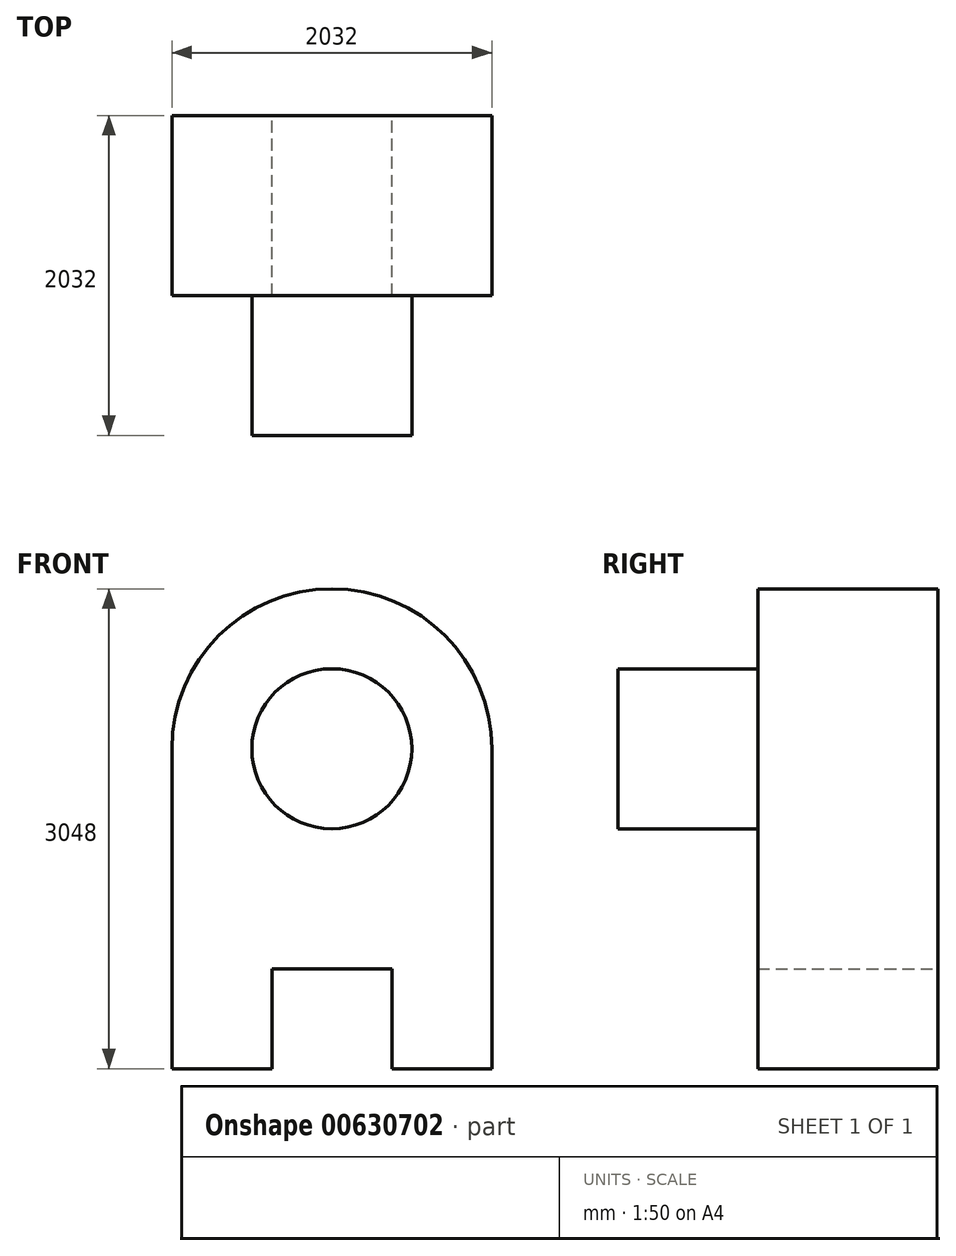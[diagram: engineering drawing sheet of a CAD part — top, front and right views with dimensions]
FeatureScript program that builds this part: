
annotation { "Feature Type Name" : "Feature", "Feature Type Description" : "" }
export const myFeature = defineFeature(function(context is Context, id is Id, definition is map)
    precondition{}
    {
        {
            var Q0;
            Q0=qCreatedBy(makeId("Front.planeOp"),FACE);
            var sketch = newSketch(context, id + "F0", { "sketchPlane" : qUnion([Q0])});
            skLineSegment(sketch, "E0.bottom", {"start": v(-1016, -1016) * mm, "end": v(-381, -1016) * mm});
            skLineSegment(sketch, "E0.left", {"start": v(-1016, -1016) * mm, "end": v(-1016, 1016) * mm});
            skLineSegment(sketch, "E0.right", {"start": v(1016, -1016) * mm, "end": v(1016, 1016) * mm});
            skPoint(sketch, "E0.middle", {"position": v(0, 0) * mm});
            skArc(sketch, "E1", {"start": v(1016, 1016) * mm, "mid": v(0, 2032) * mm, "end": v(-1016, 1016) * mm});
            skLineSegment(sketch, "E2.top", {"start": v(-381, -381) * mm, "end": v(381, -381) * mm});
            skLineSegment(sketch, "E2.left", {"start": v(-381, -1016) * mm, "end": v(-381, -381) * mm});
            skLineSegment(sketch, "E2.right", {"start": v(381, -1016) * mm, "end": v(381, -381) * mm});
            skPoint(sketch, "E2.middle", {"position": v(0, -1016) * mm});
            skPoint(sketch, "E2.bottom.end.orphan", {"position": v(381, -1651) * mm});
            skLineSegment(sketch, "E3.trimOffspring", {"start": v(381, -1016) * mm, "end": v(1016, -1016) * mm});
            skPoint(sketch, "E4.orphan", {"position": v(-381, -1651) * mm});
            skSolve(sketch);
        }
        {
            var Q0;
            Q0 = qSketchRegion(id + "F0", true);
            extrude(context, id + "F1", {"entities" : qUnion([Q0]), "depth" : 1143 * mm, "offsetDistance" : 25.4 * mm});
        }
        {
            var Q0;
            Q0=makeQuery(id+"F1.opExtrude","CAP_FACE",FACE,{"disambiguationData":[OSD([sQuery(id+"F0.wireOp",EDGE,"E0.bottom"),sQuery(id+"F0.wireOp",EDGE,"E0.left"),sQuery(id+"F0.wireOp",EDGE,"E0.right"),sQuery(id+"F0.wireOp",EDGE,"E1"),sQuery(id+"F0.wireOp",EDGE,"E2.top"),sQuery(id+"F0.wireOp",EDGE,"E2.left"),sQuery(id+"F0.wireOp",EDGE,"E2.right"),sQuery(id+"F0.wireOp",EDGE,"E3.trimOffspring")])],"isStart":false});
            var sketch = newSketch(context, id + "F2", { "sketchPlane" : qUnion([Q0])});
            skCircle(sketch, "E5", {"center": v(0, 1016) * mm, "radius": 508 * mm});
            skSolve(sketch);
        }
        {
            var Q0;
            Q0 = qSketchRegion(id + "F2", true);
            extrude(context, id + "F3", {"entities" : qUnion([Q0]), "operationType" : NewBodyOperationType.ADD, "depth" : 889 * mm, "offsetDistance" : 25.4 * mm});
        }
    });
